# Revit family: Lighting_Fixture-Luminii-Downlight-Atto_Eye new
name_source: partatom
category: Lighting Fixtures
units: mm (PartAtom-declared; Revit-internal decimal feet)

## family parameters
Cut with Voids When Loaded = No
Host = Face
Light Source = Yes
OmniClass Number = 23.80.70.11.14.11
OmniClass Title = Downlights
Part Type = Normal
Room Calculation Point = No
Round Connector Dimension = Use Diameter
Shared = Yes

## types (8) — shared parameters
Apparent Load = 1 VA
Assembly Code = D5020200
Color Filter = 16777215
Control Type = Consult Manufacturer Website for more Information
Control Zone = Consult Manufacturer Website for more Information
Current Amps = 0 A
Default Elevation = 0"
Description = Single Source LED Recessed Spotlight
Diameter = 1 1/4"
Dimming Lamp Color Temperature Shift = <None>
Dimming Type = DALI | 0-10V | 1-10V | Casambi
Environment = Indoor
Finish = Metal - Luminii - White
Frequency = 60 Hz
Has Battery Backup = No
Has Dimming = Yes
Height = 7/8"
Housing Protection Rating = Consult Manufacturer Website for more Information
Initial Color Comments = Perfomance based on Photometric Web File
Keynote = 26 51 00
Lamp = LED
Lamp Life = 1
Lens Material = Plastic - Luminii - Frosted Lens
Load Classification = Lighting
Luminaire Type = Single Source LED Recessed Spotlight
Manufacturer = Luminii
Material = Standard: White, Black, Brushed Aluminum. Premium: Rubbed Bronze, Polished Brass, Brushed Brass.
Model = 764
Mounting Method = Recessed Mount
Number of Poles = 1
Operating Temperature = Consult Manufacturer Website for more Information
Phase = 1
Power Factor = 1
Power Source Type = Driver
Product Page URL = https://www.luminii.com
Tilt Angle = 90.00°
URL = https://www.luminii.com
Version = 2020 - v1.0a
Voltage = 120 V
Voltage Comments = 120V | 230V
Warranty URL = https://www.luminii.com
Wattage Comments = 1.12 W

## per-type parameters (varying)
| type | CCT | Distribution | Lumen Output | Photometric Web File |
| Atto Eye - 2700K 95 CRI Narrow Beam | 2700K | Flood Beam 45° | Nominal 102lm, Delivered 94lm | 760-16.IES |
| Atto Eye - 3000K 95 CRI Narrow Beam | 3000K | Narrow Beam 16° | Nominal 102lm, Delivered 94lm | 760-16.IES |
| Atto Eye - 2700K 95 CRI Medium Beam | 2700K | Medium Beam 23° | Nominal 102lm, Delivered 92lm | 760-23.IES |
| Atto Eye - 3000K 95 CRI Medium Beam | 3000K | Medium Beam 23° | Nominal 102lm, Delivered 92lm | 760-23.IES |
| Atto Eye - 2700K 95 CRI Flood Beam | 2700K | Flood Beam 45° | Nominal 102lm, Delivered 93lm | 760-45.IES |
| Atto Eye - 3000K 95 CRI Flood Beam | 3000K | Flood Beam 45° | Nominal 102lm, Delivered 93lm | 760-45.IES |
| Atto Eye - 2700K 95 CRI Wide Flood Beam | 2700K | Wide Flood Beam 90° | Nominal 102lm, Delivered 69lm | 760-90.ies |
| Atto Eye - 3000K 95 CRI Wide Flood Beam | 3000K | Wide Flood Beam 90° | Nominal 102lm, Delivered 69lm | 760-90.ies |

## geometry (parser evidence)
native form markers: Sweep x4
no freeform markers — native parametric forms only
